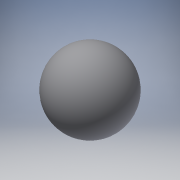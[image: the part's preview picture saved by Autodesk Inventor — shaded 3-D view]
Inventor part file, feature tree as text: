
AUTODESK INVENTOR PART (.ipt)
format: ipt  version: 2016 (Build 200138000, 138)  size: 123,904 bytes
history: native  units: mm
features: revolve x1, sketch x1
ambient origin geometry x8: Origin, YZ Plane, XZ Plane, XY Plane, X Axis, Y Axis, Z Axis, Center Point
bodies: Solid1 (feature_tree)
feature tree (2):
  revolve  "Revolution1"  Angle=90.0deg
  sketch  "Sketch1"  dims[d0=500.0mm d1=90.0deg]
